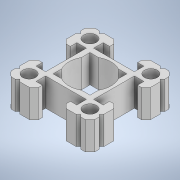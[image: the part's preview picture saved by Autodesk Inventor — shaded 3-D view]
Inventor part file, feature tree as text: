
AUTODESK INVENTOR PART (.ipt)
format: ipt  version: 2020 (Build 240168000, 168)  size: 3,237,376 bytes
history: mixed  units: in
note: dims shown in document units (in); Inventor stores cm internally (conversion verified against a paired STEP export)
features: extrude x1, sketch x1, imported_body x1
ambient origin geometry x8: Origin, YZ Plane, XZ Plane, XY Plane, X Axis, Y Axis, Z Axis, Center Point
bodies: Solid1 (imported_parasolid)
feature tree (3):
  extrude  "Extrusion1"  Depth=2.4375in TaperAngle=0.0deg
  sketch  "Sketch1"  dims[d0=5.75in d1=2.4375in d2=0.0in]
  imported_body  NMx_Import_Brep_tag  [imported B-rep: ~90 faces, bbox_mm=[19.05, 6.35, 19.05]]
